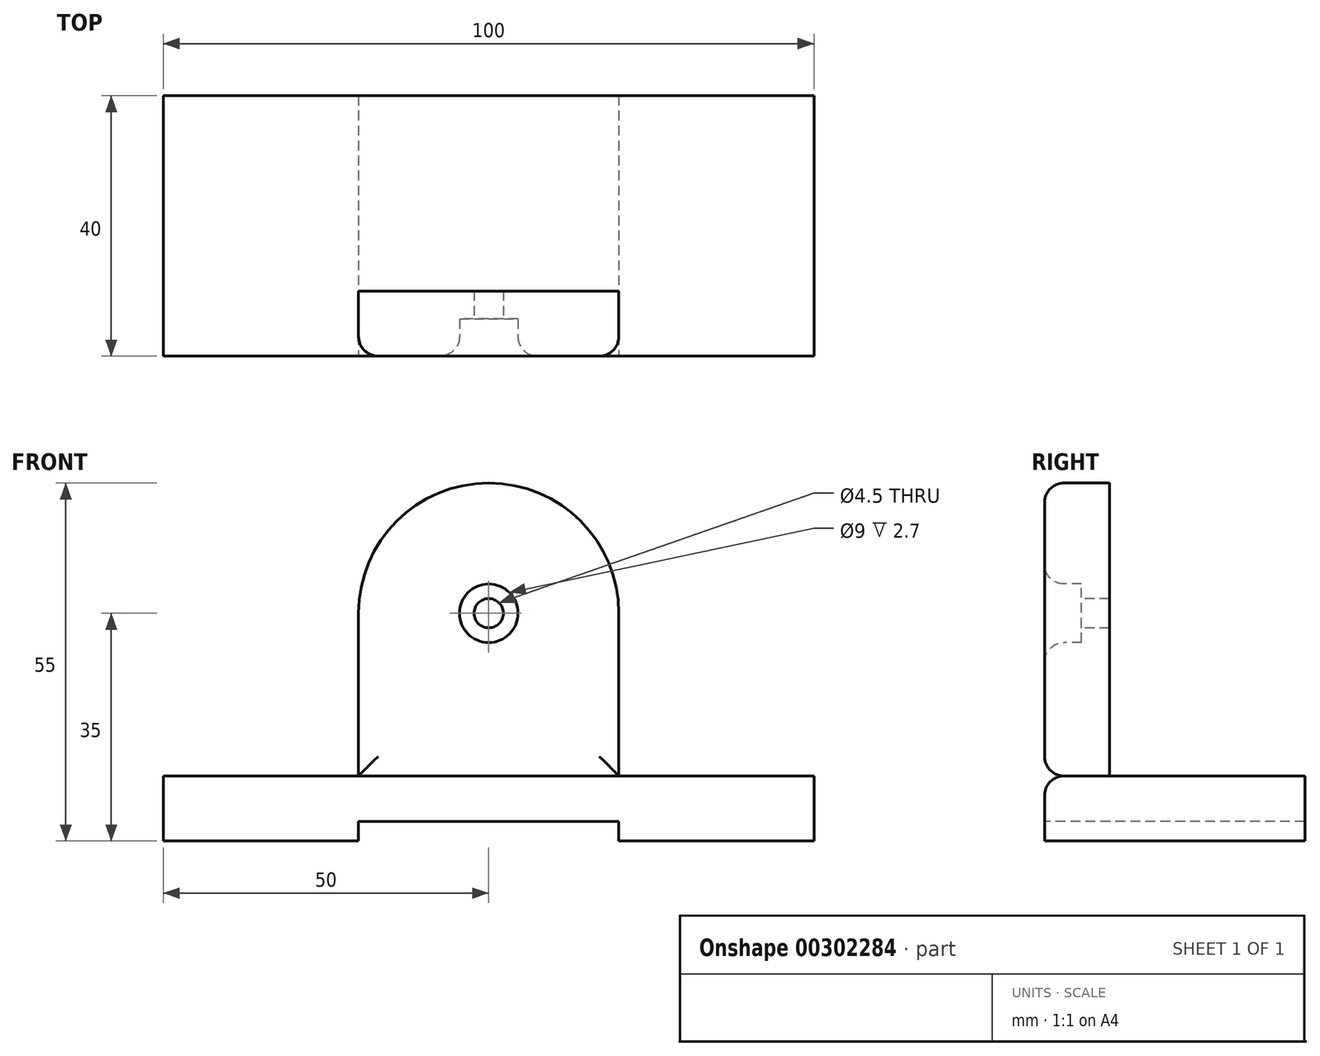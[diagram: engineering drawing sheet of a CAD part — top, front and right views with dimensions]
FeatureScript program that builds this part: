
annotation { "Feature Type Name" : "Feature", "Feature Type Description" : "" }
export const myFeature = defineFeature(function(context is Context, id is Id, definition is map)
    precondition{}
    {
        {
            var Q0;
            Q0=qCreatedBy(makeId("Top.planeOp"),FACE);
            var sketch = newSketch(context, id + "F0", { "sketchPlane" : qUnion([Q0])});
            skLineSegment(sketch, "E0.bottom", {"start": v(0, 0) * mm, "end": v(-100, 0) * mm});
            skLineSegment(sketch, "E0.top", {"start": v(0, 40) * mm, "end": v(-100, 40) * mm});
            skLineSegment(sketch, "E0.left", {"start": v(0, 0) * mm, "end": v(0, 40) * mm});
            skLineSegment(sketch, "E0.right", {"start": v(-100, 0) * mm, "end": v(-100, 40) * mm});
            skSolve(sketch);
        }
        {
            var Q0;
            Q0 = qSketchRegion(id + "F0", true);
            extrude(context, id + "F1", {"entities" : qUnion([Q0]), "depth" : 10 * mm});
        }
        {
            var Q0;
            Q0=makeQuery(id+"F1.opExtrude","SWEPT_FACE",FACE,{"disambiguationData":[OSD([sQuery(id+"F0.wireOp",EDGE,"E0.bottom")])]});
            var sketch = newSketch(context, id + "F2", { "sketchPlane" : qUnion([Q0])});
            skLineSegment(sketch, "E1", {"start": v(-70, 0) * mm, "end": v(-70, 35) * mm});
            skArc(sketch, "E2", {"start": v(-30, 35) * mm, "mid": v(-50, 55) * mm, "end": v(-70, 35) * mm});
            skLineSegment(sketch, "E3", {"start": v(-30, 35) * mm, "end": v(-30, 0) * mm});
            skSolve(sketch);
        }
        {
            var Q0;
            {var subQ0=sQuery(id+"F2.wireOp",EDGE,"E2");Q0=makeQuery(id+"F2.imprint","IMPRINT",FACE,{"disambiguationData":[TD([[makeQuery(id+"F2.imprint","IMPRINT",EDGE,{"derivedFrom":subQ0}),1.0]])]});}
            extrude(context, id + "F3", {"entities" : qUnion([Q0]), "oppositeDirection" : true, "depth" : 10 * mm});
        }
        {
            var Q0;
            Q0=makeQuery(id+"F3.opExtrude","CAP_FACE",FACE,{"disambiguationData":[OSD([sQuery(id+"F0.wireOp",EDGE,"E0.bottom"),sQuery(id+"F2.wireOp",EDGE,"E1"),sQuery(id+"F2.wireOp",EDGE,"E2"),sQuery(id+"F2.wireOp",EDGE,"E3")])],"isStart":true});
            var sketch = newSketch(context, id + "F4", { "sketchPlane" : qUnion([Q0])});
            skLineSegment(sketch, "E4.bottom", {"start": v(-70, 3) * mm, "end": v(-30, 3) * mm});
            skLineSegment(sketch, "E4.top", {"start": v(-70, 0) * mm, "end": v(-30, 0) * mm});
            skLineSegment(sketch, "E4.left", {"start": v(-70, 3) * mm, "end": v(-70, 0) * mm});
            skLineSegment(sketch, "E4.right", {"start": v(-30, 3) * mm, "end": v(-30, 0) * mm});
            skSolve(sketch);
        }
        {
            var Q0;
            Q0 = qSketchRegion(id + "F4", true);
            extrude(context, id + "F5", {"entities" : qUnion([Q0]), "operationType" : NewBodyOperationType.REMOVE, "endBound" : BoundingType.THROUGH_ALL, "oppositeDirection" : true, "depth" : 25 * mm});
        }
        {
            var Q0;
            Q0=makeQuery(id+"F3.opExtrude","CAP_FACE",FACE,{"disambiguationData":[OSD([sQuery(id+"F0.wireOp",EDGE,"E0.bottom"),sQuery(id+"F2.wireOp",EDGE,"E1"),sQuery(id+"F2.wireOp",EDGE,"E2"),sQuery(id+"F2.wireOp",EDGE,"E3")])],"isStart":true});
            var sketch = newSketch(context, id + "F6", { "sketchPlane" : qUnion([Q0])});
            skCircle(sketch, "E5", {"center": v(-50, 35) * mm, "radius": 2.25 * mm});
            skSolve(sketch);
        }
        {
            var Q0;
            Q0 = qSketchRegion(id + "F6", true);
            extrude(context, id + "F7", {"entities" : qUnion([Q0]), "operationType" : NewBodyOperationType.REMOVE, "endBound" : BoundingType.THROUGH_ALL, "oppositeDirection" : true, "depth" : 25 * mm});
        }
        {
            var Q0;
            Q0=makeQuery(id+"F3.opExtrude","CAP_FACE",FACE,{"disambiguationData":[OSD([sQuery(id+"F0.wireOp",EDGE,"E0.bottom"),sQuery(id+"F2.wireOp",EDGE,"E1"),sQuery(id+"F2.wireOp",EDGE,"E2"),sQuery(id+"F2.wireOp",EDGE,"E3")])],"isStart":true});
            var sketch = newSketch(context, id + "F8", { "sketchPlane" : qUnion([Q0])});
            skCircle(sketch, "E6", {"center": v(-50, 35) * mm, "radius": 4.5 * mm});
            skSolve(sketch);
        }
        {
            var Q0;
            Q0 = qSketchRegion(id + "F8", true);
            extrude(context, id + "F9", {"entities" : qUnion([Q0]), "operationType" : NewBodyOperationType.REMOVE, "oppositeDirection" : true, "depth" : 5.7 * mm});
        }
        {
            var Q0;
            Q0=makeQuery(id+"F3.opExtrude","CAP_FACE",FACE,{"disambiguationData":[OSD([sQuery(id+"F0.wireOp",EDGE,"E0.bottom"),sQuery(id+"F2.wireOp",EDGE,"E1"),sQuery(id+"F2.wireOp",EDGE,"E2"),sQuery(id+"F2.wireOp",EDGE,"E3")])],"isStart":true});
            fillet(context, id + "F10", {"entities" : qUnion([Q0]), "radius" : 3 * mm, "tangentPropagation" : true, "allowEdgeOverflow" : false});
        }
        {
            var Q0;
            Q0=makeQuery(id+"F1.opExtrude","CAP_EDGE",EDGE,{"disambiguationData":[OSD([sQuery(id+"F0.wireOp",EDGE,"E0.bottom")])],"isStart":false});
            fillet(context, id + "F11", {"entities" : qUnion([Q0]), "radius" : 3 * mm, "tangentPropagation" : true, "allowEdgeOverflow" : false});
        }
    });
